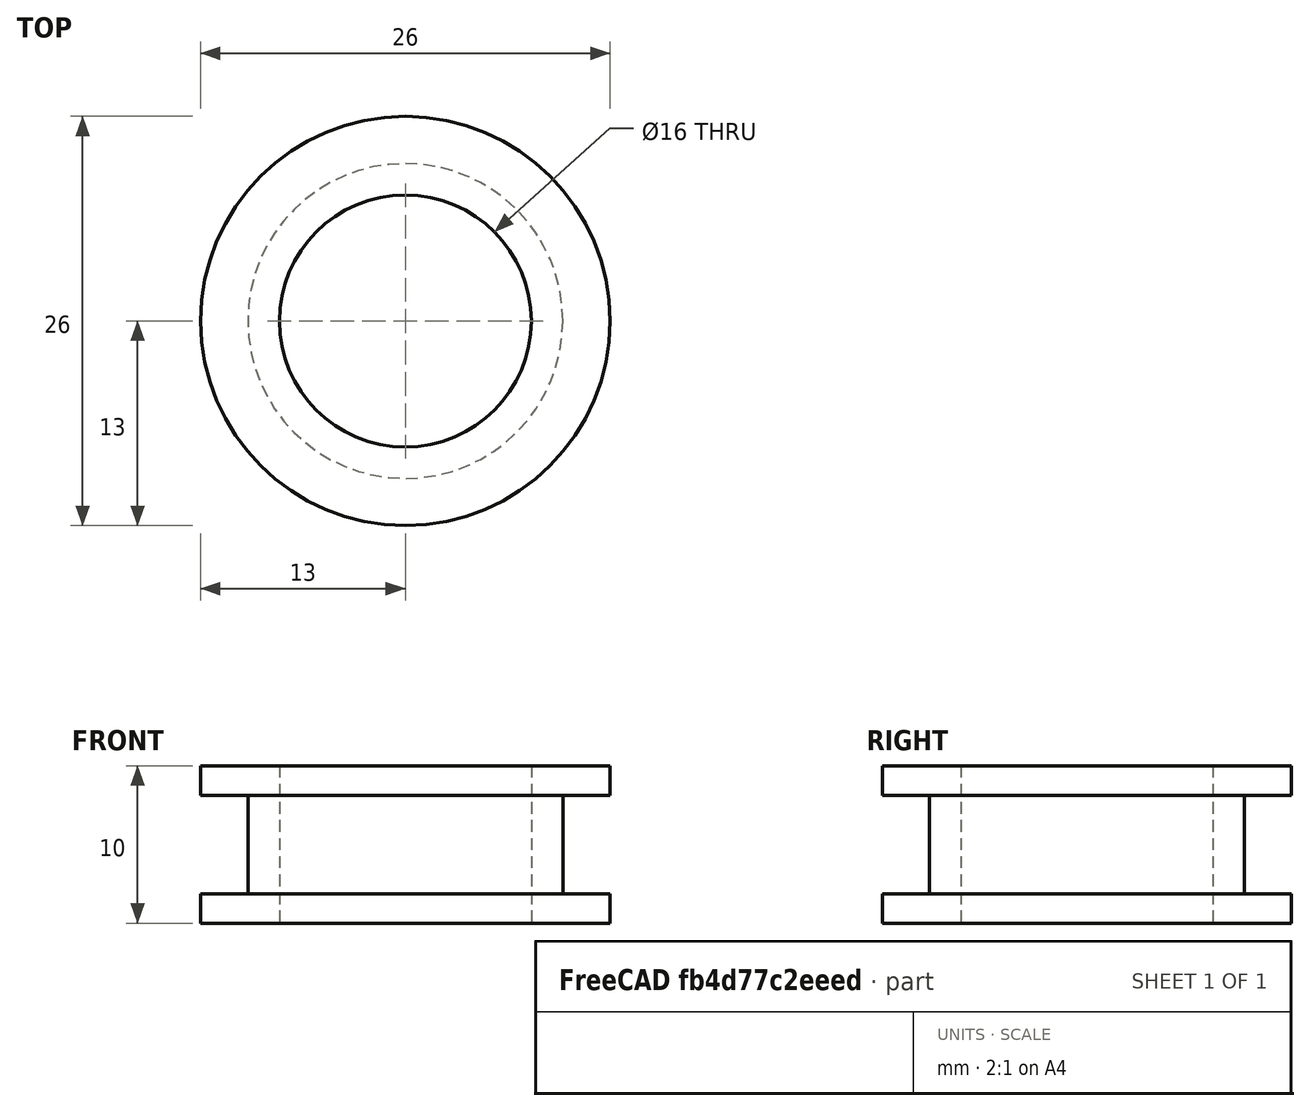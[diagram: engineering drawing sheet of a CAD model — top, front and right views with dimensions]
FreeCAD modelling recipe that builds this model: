
FCSTD DOCUMENT  (FreeCAD 0.19R)
Label: x-axis-pulley
License: All rights reserved
LicenseURL: http://en.wikipedia.org/wiki/All_rights_reserved
objects: Sketcher::SketchObject×1, PartDesign::Revolution×1, PartDesign::Body×1
note: 4 computed .brp shape members not serialized (recipe doc carries the construction recipe); baked Part::Feature solids carry a one-line shape summary decoded from their .brp

FEATURE [Sketcher::SketchObject] Sketch
  FullyConstrained = true
  MapMode = 5
  Placement = pos=(0,0,0) rot=(1,0,0;1.5708rad)
  Support = -> [XZ_Plane]
  sketch-geometry (8):
    g0: LineSegment StartX=8 StartY=10 StartZ=0 EndX=8 EndY=0 EndZ=0
    g1: LineSegment StartX=8 StartY=10 StartZ=0 EndX=13 EndY=10 EndZ=0
    g2: LineSegment StartX=13 StartY=10 StartZ=0 EndX=13 EndY=8.125 EndZ=0
    g3: LineSegment StartX=13 StartY=8.125 StartZ=0 EndX=10 EndY=8.125 EndZ=0
    g4: LineSegment StartX=10 StartY=8.125 StartZ=0 EndX=10 EndY=1.875 EndZ=0
    g5: LineSegment StartX=10 StartY=1.875 StartZ=0 EndX=13 EndY=1.875 EndZ=0
    g6: LineSegment StartX=13 StartY=1.875 StartZ=0 EndX=13 EndY=0 EndZ=0
    g7: LineSegment StartX=13 StartY=0 StartZ=0 EndX=8 EndY=0 EndZ=0
  constraints (24):
    c: PointOnObject(g0,g-1)
    c: Vertical(g0)
    c: Coincident(g1,g0)
    c: Horizontal(g1)
    c: Coincident(g2,g1)
    c: Vertical(g2)
    c: Coincident(g3,g2)
    c: Horizontal(g3)
    c: Coincident(g4,g3)
    c: Vertical(g4)
    c: Coincident(g5,g4)
    c: Horizontal(g5)
    c: Coincident(g6,g5)
    c: PointOnObject(g6,g-1)
    c: Vertical(g6)
    c: Coincident(g7,g6)
    c: Coincident(g7,g0)
    c: Equal(g6,g2)
    c: Equal(g3,g5)
    c: DistanceY(g4,g4) = 6.25
    c: DistanceX(g3,g3) = 3
    c: DistanceX(g0,g3) = 2
    c: DistanceX(g-1,g0) = 8
    c: DistanceY(g0,g0) = 10
FEATURE [PartDesign::Revolution] Revolution
  Angle = 360
  Axis = (0,2e-16,1)
  Base = (0,0,0)
  Placement = pos=(0,0,0) rot=(1,0,0;1.5708rad)
  Profile = -> Sketch
  ReferenceAxis = -> Sketch [V_Axis]
  Reversed = true
FEATURE [PartDesign::Body] Body
  Group = -> [Sketch,Revolution]
  Origin = -> Origin
  Tip = -> Revolution
